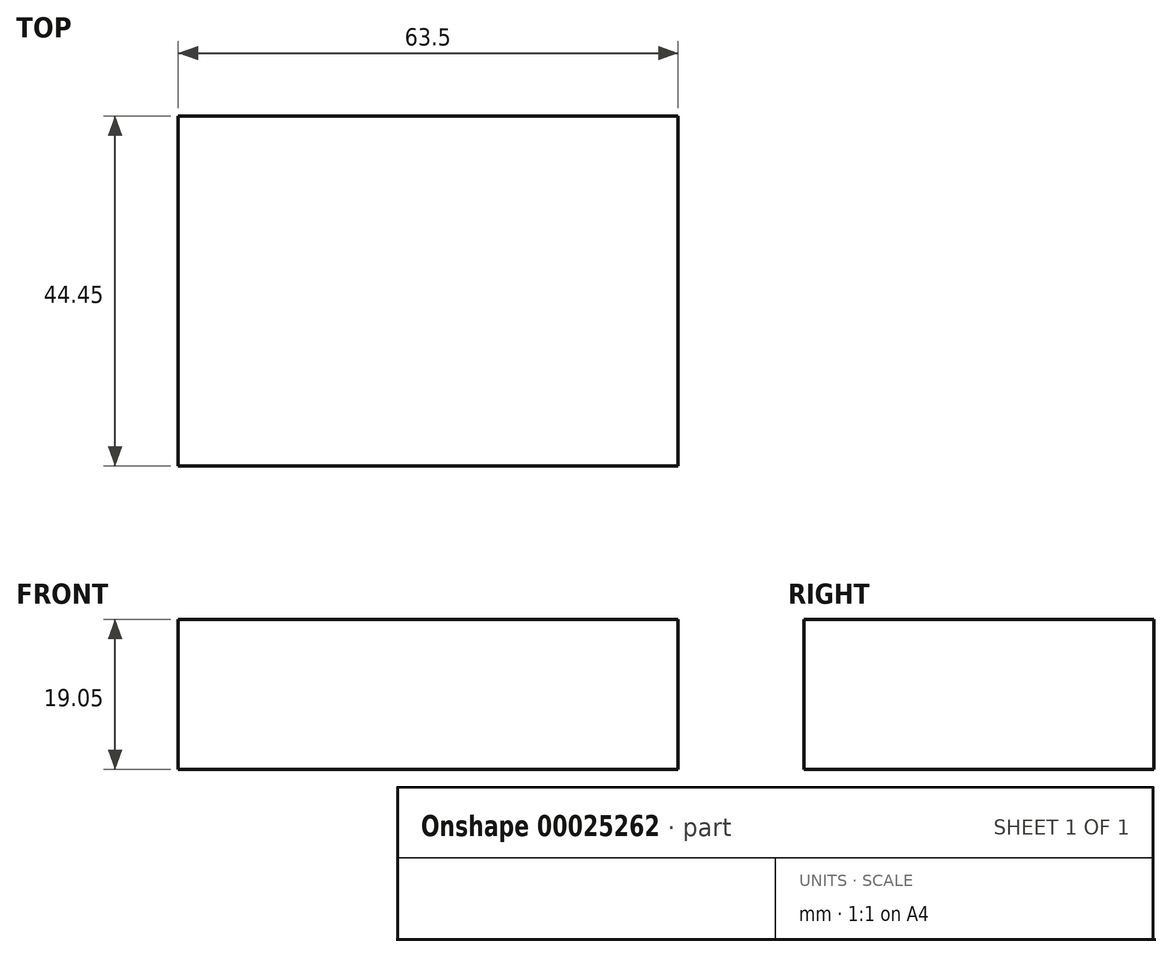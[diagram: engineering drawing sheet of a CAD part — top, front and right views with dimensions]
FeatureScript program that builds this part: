
annotation { "Feature Type Name" : "Feature", "Feature Type Description" : "" }
export const myFeature = defineFeature(function(context is Context, id is Id, definition is map)
    precondition{}
    {
        {
            var Q0;
            Q0=qCreatedBy(makeId("Front.planeOp"),FACE);
            var sketch = newSketch(context, id + "F0", { "sketchPlane" : qUnion([Q0])});
            skLineSegment(sketch, "E0", {"start": v(-22.18, 21.99) * mm, "end": v(-22.18, 2.94) * mm});
            skLineSegment(sketch, "E1", {"start": v(-22.18, 2.94) * mm, "end": v(41.32, 2.94) * mm});
            skLineSegment(sketch, "E2", {"start": v(41.32, 2.94) * mm, "end": v(41.32, 21.99) * mm});
            skLineSegment(sketch, "E3", {"start": v(41.32, 21.99) * mm, "end": v(-22.18, 21.99) * mm});
            skSolve(sketch);
        }
        {
            var Q0;
            Q0 = qSketchRegion(id + "F0", true);
            extrude(context, id + "F1", {"entities" : qUnion([Q0]), "depth" : 44.45 * mm});
        }
    });
